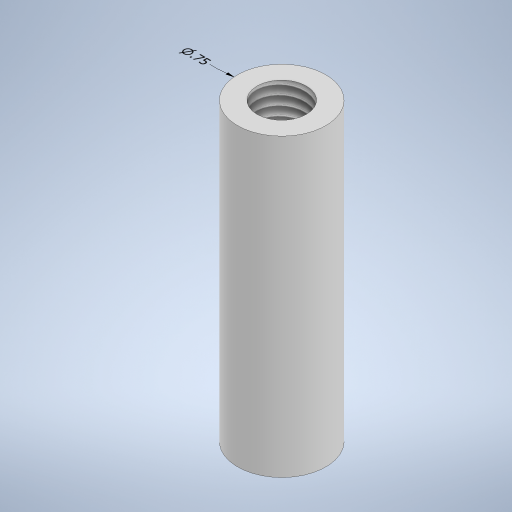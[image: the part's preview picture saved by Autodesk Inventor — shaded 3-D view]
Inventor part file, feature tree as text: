
AUTODESK INVENTOR PART (.ipt)
format: ipt  version: 2023 (Build 270158000, 158)  size: 249,344 bytes
history: native  units: in
note: dims shown in document units (in); Inventor stores cm internally (conversion verified against a paired STEP export)
features: other x2, sketch x2, extrude x1, hole x1
ambient origin geometry x8: Origin, YZ Plane, XZ Plane, XY Plane, X Axis, Y Axis, Z Axis, Center Point
bodies: Solid1 (feature_tree)
feature tree (6):
  other  "Annotations"
  extrude  "Extrusion1"  Depth=2.5in TaperAngle=0.0deg
  hole  "Hole1"  [1 undecoded]
  sketch  "Sketch1"  dims[d0=0.746in d1=2.5in d2=0.0in]
  sketch  "Sketch3"  dims[d10=0.5in d11=0.417in d12=1.0in d13=0.375in d14=0.25in d15=0.5635in d16=1.385in d17=0.8108in d8=0.0331in d9=0.746in]
  other  "Diameter Dimension 1"
note: 1 required parameter value undecoded (feature->parameter linkage not recoverable at this tier; creation-order binding heuristic only, values carry confidence <= 0.55)
